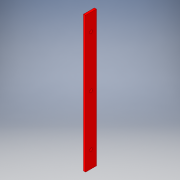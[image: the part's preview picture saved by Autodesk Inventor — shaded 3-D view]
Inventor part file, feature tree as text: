
AUTODESK INVENTOR PART (.ipt)
format: ipt  version: 2019 (Build 230136000, 136)  size: 105,984 bytes
history: native  units: mm
features: extrude x1, sketch x1
ambient origin geometry x8: Origin, YZ Plane, XZ Plane, XY Plane, X Axis, Y Axis, Z Axis, Center Point
bodies: Body1 (feature_tree)
feature tree (2):
  extrude  "Extrusion2"  [1 undecoded]
  sketch  "Sketch2"  dims[d2=2.0mm d3=0.0mm]
note: 1 required parameter value undecoded (feature->parameter linkage not recoverable at this tier; creation-order binding heuristic only, values carry confidence <= 0.55)
